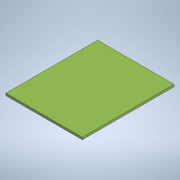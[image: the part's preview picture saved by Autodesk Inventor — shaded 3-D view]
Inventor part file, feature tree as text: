
AUTODESK INVENTOR PART (.ipt)
format: ipt  version: 2020 (Build 240168000, 168)  size: 93,696 bytes
history: native  units: mm
features: extrude x1, sketch x1
ambient origin geometry x8: Origin, YZ Plane, XZ Plane, XY Plane, X Axis, Y Axis, Z Axis, Center Point
bodies: Solid1 (feature_tree)
feature tree (2):
  extrude  "Extrusion1"  Depth=60.0mm
  sketch  "Sketch1"  dims[d0=50.0mm d1=60.0mm d2=1.5mm d3=0.0mm]
